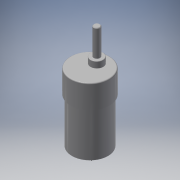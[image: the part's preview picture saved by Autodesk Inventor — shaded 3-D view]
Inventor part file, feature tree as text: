
AUTODESK INVENTOR PART (.ipt)
format: ipt  version: 2016 (Build 200138000, 138)  size: 210,944 bytes
history: native  units: in
note: dims shown in document units (in); Inventor stores cm internally (conversion verified against a paired STEP export)
features: fillet x1
ambient origin geometry x8: Origin, YZ Plane, XZ Plane, XY Plane, X Axis, Y Axis, Z Axis, Center Point
bodies: Solid1 (feature_tree)
feature tree (1):
  fillet  "Fillet2"  [1 undecoded]
note: 1 required parameter value undecoded (feature->parameter linkage not recoverable at this tier; creation-order binding heuristic only, values carry confidence <= 0.55)
